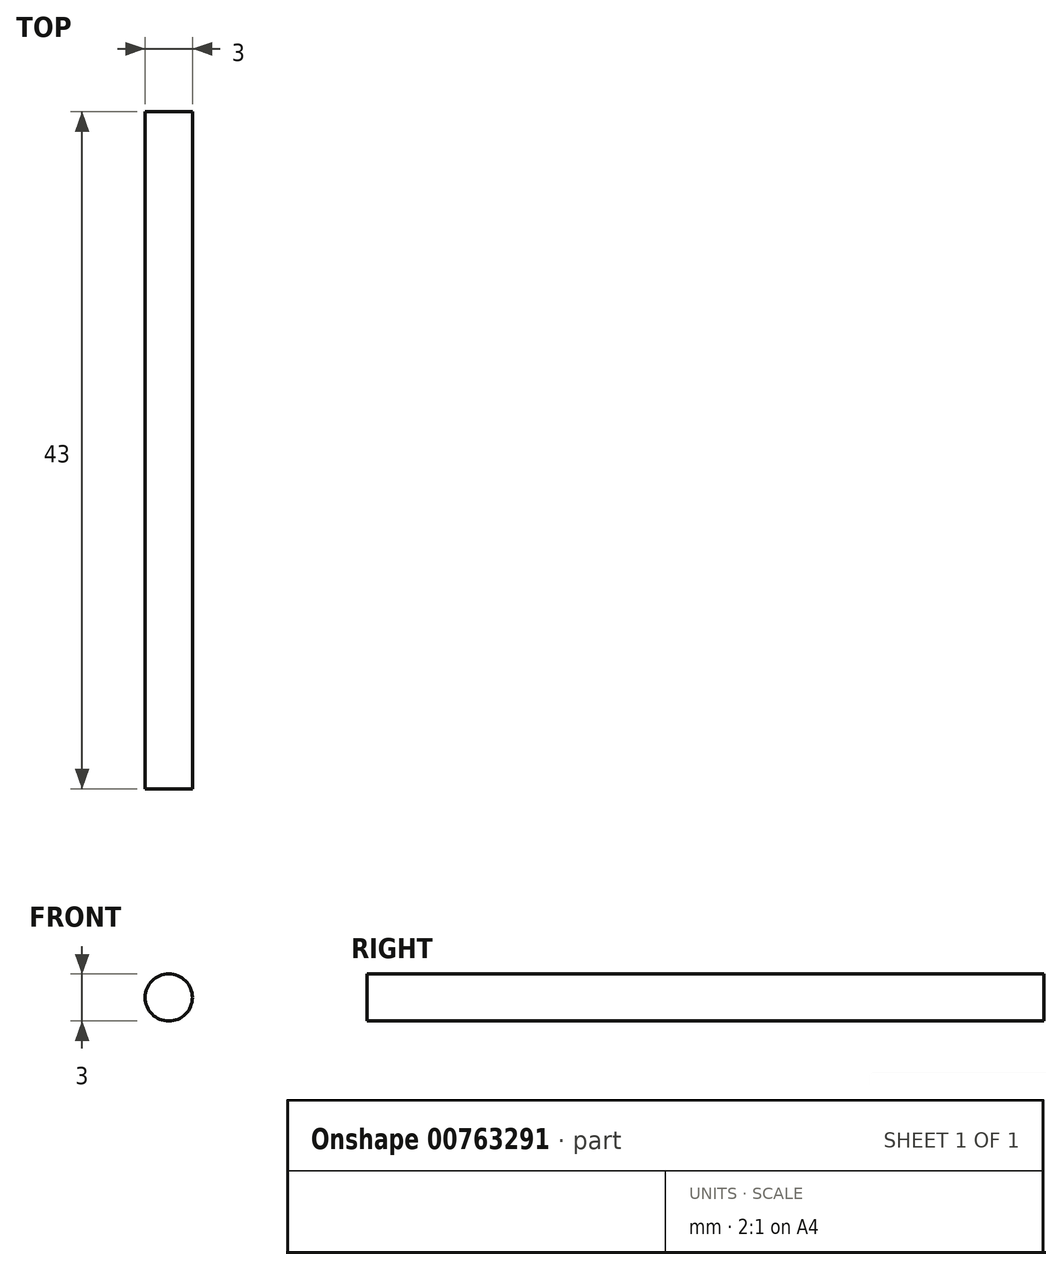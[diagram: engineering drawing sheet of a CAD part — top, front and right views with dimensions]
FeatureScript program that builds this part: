
annotation { "Feature Type Name" : "Feature", "Feature Type Description" : "" }
export const myFeature = defineFeature(function(context is Context, id is Id, definition is map)
    precondition{}
    {
        {
            var Q0;
            Q0=qCreatedBy(makeId("Front.planeOp"),FACE);
            var sketch = newSketch(context, id + "F0", { "sketchPlane" : qUnion([Q0])});
            skCircle(sketch, "E0", {"center": v(0, 0) * mm, "radius": 1.5 * mm});
            skSolve(sketch);
        }
        {
            var Q0;
            Q0=makeQuery(id+"F0.imprint","IMPRINT",FACE,{"disambiguationData":[TD([[makeQuery(id+"F0.imprint","IMPRINT",EDGE,{"derivedFrom":sQuery(id+"F0.wireOp",EDGE,"E0")}),1.0]])]});
            extrude(context, id + "F1", {"entities" : qUnion([Q0]), "depth" : 43 * mm, "offsetDistance" : 25 * mm});
        }
    });
